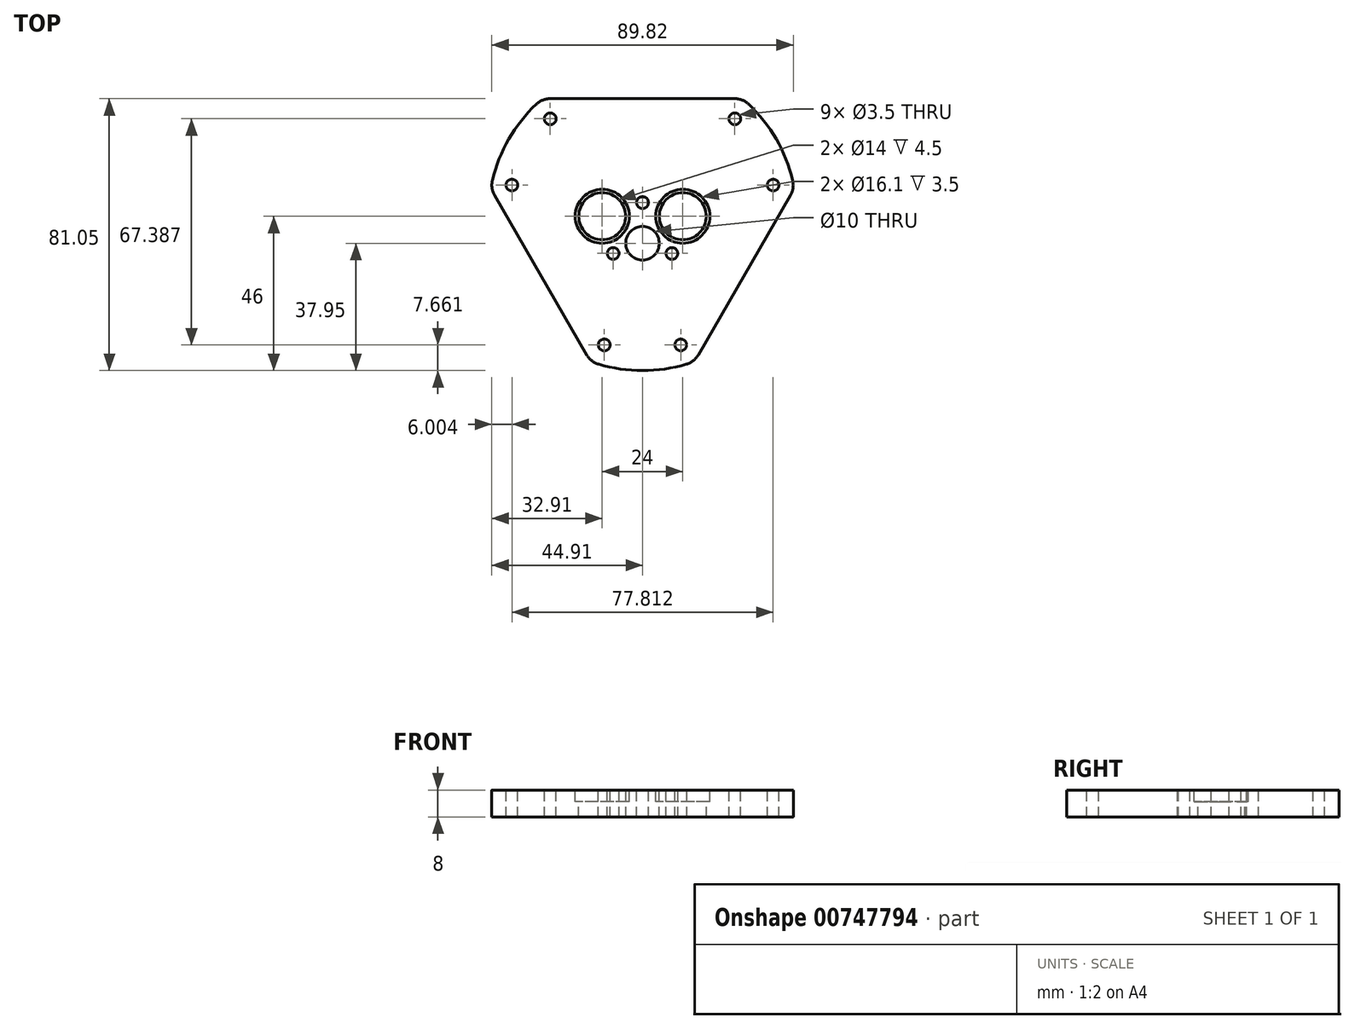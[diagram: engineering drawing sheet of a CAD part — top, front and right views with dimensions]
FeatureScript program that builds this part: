
annotation { "Feature Type Name" : "Feature", "Feature Type Description" : "" }
export const myFeature = defineFeature(function(context is Context, id is Id, definition is map)
    precondition{}
    {
        {
            var Q0;
            Q0=qCreatedBy(makeId("Top.planeOp"),FACE);
            var sketch = newSketch(context, id + "F0", { "sketchPlane" : qUnion([Q0])});
            skCircle(sketch, "E0", {"center": v(-12, 0) * mm, "radius": 7 * mm});
            skCircle(sketch, "E1", {"center": v(-12, 0) * mm, "radius": 8.05 * mm});
            skCircle(sketch, "E2", {"center": v(12, 0) * mm, "radius": 7 * mm});
            skCircle(sketch, "E3", {"center": v(12, 0) * mm, "radius": 8.05 * mm});
            skLineSegment(sketch, "E4.0", {"start": v(8.75, -11.08) * mm, "end": v(-8.75, -11.08) * mm, "construction": true});
            skLineSegment(sketch, "E4.1", {"start": v(-8.75, -11.08) * mm, "end": v(0, 4.07) * mm, "construction": true});
            skLineSegment(sketch, "E4.2", {"start": v(0, 4.07) * mm, "end": v(8.75, -11.08) * mm, "construction": true});
            skPoint(sketch, "E4.0.midPoint", {"position": v(0, -11.08) * mm});
            skCircle(sketch, "E5", {"center": v(8.75, -11.08) * mm, "radius": 1.75 * mm});
            skCircle(sketch, "E6", {"center": v(-8.75, -11.08) * mm, "radius": 1.75 * mm});
            skCircle(sketch, "E7", {"center": v(0, 4.07) * mm, "radius": 1.75 * mm});
            skCircle(sketch, "E8", {"center": v(0, -8.05) * mm, "radius": 5 * mm});
            skCircle(sketch, "E9", {"center": v(-38.9, 9.3) * mm, "radius": 1.75 * mm});
            skCircle(sketch, "E10", {"center": v(-38.9, 9.3) * mm, "radius": 6 * mm});
            skCircle(sketch, "E11", {"center": v(-11.4, -38.34) * mm, "radius": 1.75 * mm});
            skCircle(sketch, "E12", {"center": v(-11.4, -38.34) * mm, "radius": 6 * mm});
            skCircle(sketch, "E13", {"center": v(11.4, -38.34) * mm, "radius": 6 * mm});
            skCircle(sketch, "E14", {"center": v(11.4, -38.34) * mm, "radius": 1.75 * mm});
            skCircle(sketch, "E15", {"center": v(38.9, 9.3) * mm, "radius": 1.75 * mm});
            skCircle(sketch, "E16", {"center": v(38.9, 9.3) * mm, "radius": 6 * mm});
            skCircle(sketch, "E17", {"center": v(-27.5, 29.05) * mm, "radius": 1.75 * mm});
            skCircle(sketch, "E18", {"center": v(-27.5, 29.05) * mm, "radius": 6 * mm});
            skCircle(sketch, "E19", {"center": v(27.5, 29.05) * mm, "radius": 1.75 * mm});
            skCircle(sketch, "E20", {"center": v(27.5, 29.05) * mm, "radius": 6 * mm});
            skLineSegment(sketch, "E21", {"start": v(-27.5, 29.05) * mm, "end": v(27.5, 29.05) * mm});
            skLineSegment(sketch, "E22", {"start": v(38.9, 9.3) * mm, "end": v(11.4, -38.34) * mm, "construction": true});
            skLineSegment(sketch, "E23", {"start": v(-11.4, -38.34) * mm, "end": v(-38.9, 9.3) * mm});
            skCircle(sketch, "E24", {"center": v(0, 0) * mm, "radius": 40 * mm, "construction": true});
            skCircle(sketch, "E25", {"center": v(0, 0) * mm, "radius": 46 * mm});
            skLineSegment(sketch, "E26", {"start": v(-44.1, 6.3) * mm, "end": v(-16.6, -41.34) * mm});
            skLineSegment(sketch, "E27", {"start": v(16.6, -41.34) * mm, "end": v(44.1, 6.3) * mm});
            skLineSegment(sketch, "E28", {"start": v(27.5, 35.05) * mm, "end": v(-27.5, 35.05) * mm});
            skLineSegment(sketch, "E29", {"start": v(-12, -8.05) * mm, "end": v(12, -8.05) * mm, "construction": true});
            skLineSegment(sketch, "E30", {"start": v(-12, 0) * mm, "end": v(12, 0) * mm});
            skLineSegment(sketch, "E31", {"start": v(0, 4.07) * mm, "end": v(0, -11.08) * mm});
            skSolve(sketch);
        }
        {
            var Q0;
            Q0=makeQuery(id+"F0.imprint","IMPRINT",FACE,{"disambiguationData":[TD([[makeQuery(id+"F0.imprint","IMPRINT",EDGE,{"derivedFrom":sQuery(id+"F0.wireOp",EDGE,"E1")}),-1.0]])]});
            var Q1;
            {var subQ0=sQuery(id+"F0.wireOp",EDGE,"E26");Q1=makeQuery(id+"F0.imprint","IMPRINT",FACE,{"disambiguationData":[TD([[makeQuery(id+"F0.imprint","IMPRINT",EDGE,{"derivedFrom":subQ0}),1.0]])]});}
            var Q2;
            Q2=makeQuery(id+"F0.imprint","IMPRINT",FACE,{"disambiguationData":[TD([[makeQuery(id+"F0.imprint","IMPRINT",EDGE,{"derivedFrom":sQuery(id+"F0.wireOp",EDGE,"E9")}),-1.0]])]});
            var Q3;
            Q3=makeQuery(id+"F0.imprint","IMPRINT",FACE,{"disambiguationData":[TD([[makeQuery(id+"F0.imprint","IMPRINT",EDGE,{"derivedFrom":sQuery(id+"F0.wireOp",EDGE,"E17")}),-1.0]])]});
            var Q4;
            {var subQ0=sQuery(id+"F0.wireOp",EDGE,"E28");Q4=makeQuery(id+"F0.imprint","IMPRINT",FACE,{"disambiguationData":[TD([[makeQuery(id+"F0.imprint","IMPRINT",EDGE,{"derivedFrom":subQ0}),1.0]])]});}
            var Q5;
            Q5=makeQuery(id+"F0.imprint","IMPRINT",FACE,{"disambiguationData":[TD([[makeQuery(id+"F0.imprint","IMPRINT",EDGE,{"derivedFrom":sQuery(id+"F0.wireOp",EDGE,"E19")}),-1.0]])]});
            var Q6;
            Q6=makeQuery(id+"F0.imprint","IMPRINT",FACE,{"disambiguationData":[TD([[makeQuery(id+"F0.imprint","IMPRINT",EDGE,{"derivedFrom":sQuery(id+"F0.wireOp",EDGE,"E15")}),-1.0]])]});
            var Q7;
            Q7=makeQuery(id+"F0.imprint","IMPRINT",FACE,{"disambiguationData":[TD([[makeQuery(id+"F0.imprint","IMPRINT",EDGE,{"derivedFrom":sQuery(id+"F0.wireOp",EDGE,"E14")}),-1.0]])]});
            var Q8;
            Q8=makeQuery(id+"F0.imprint","IMPRINT",FACE,{"disambiguationData":[TD([[makeQuery(id+"F0.imprint","IMPRINT",EDGE,{"derivedFrom":sQuery(id+"F0.wireOp",EDGE,"E11")}),-1.0]])]});
            var Q9;
            Q9=makeQuery(id+"F0.imprint","IMPRINT",FACE,{"disambiguationData":[TD([[makeQuery(id+"F0.imprint","IMPRINT",EDGE,{"derivedFrom":sQuery(id+"F0.wireOp",EDGE,"E0")}),-1.0]])]});
            var Q10;
            Q10=makeQuery(id+"F0.imprint","IMPRINT",FACE,{"disambiguationData":[TD([[makeQuery(id+"F0.imprint","IMPRINT",EDGE,{"derivedFrom":sQuery(id+"F0.wireOp",EDGE,"E2")}),-1.0]])]});
            extrude(context, id + "F1", {"entities" : qUnion([Q0, Q1, Q2, Q3, Q4, Q5, Q6, Q7, Q8, Q9, Q10]), "oppositeDirection" : true, "depth" : 8 * mm, "offsetDistance" : 25 * mm});
        }
        {
            var Q0;
            Q0=makeQuery(id+"F0.imprint","IMPRINT",FACE,{"disambiguationData":[TD([[makeQuery(id+"F0.imprint","IMPRINT",EDGE,{"derivedFrom":sQuery(id+"F0.wireOp",EDGE,"E2")}),-1.0]])]});
            var Q1;
            Q1=makeQuery(id+"F0.imprint","IMPRINT",FACE,{"disambiguationData":[TD([[makeQuery(id+"F0.imprint","IMPRINT",EDGE,{"derivedFrom":sQuery(id+"F0.wireOp",EDGE,"E0")}),-1.0]])]});
            extrude(context, id + "F2", {"entities" : qUnion([Q0, Q1]), "operationType" : NewBodyOperationType.REMOVE, "oppositeDirection" : true, "depth" : 3.5 * mm, "offsetDistance" : 25 * mm});
        }
    });
